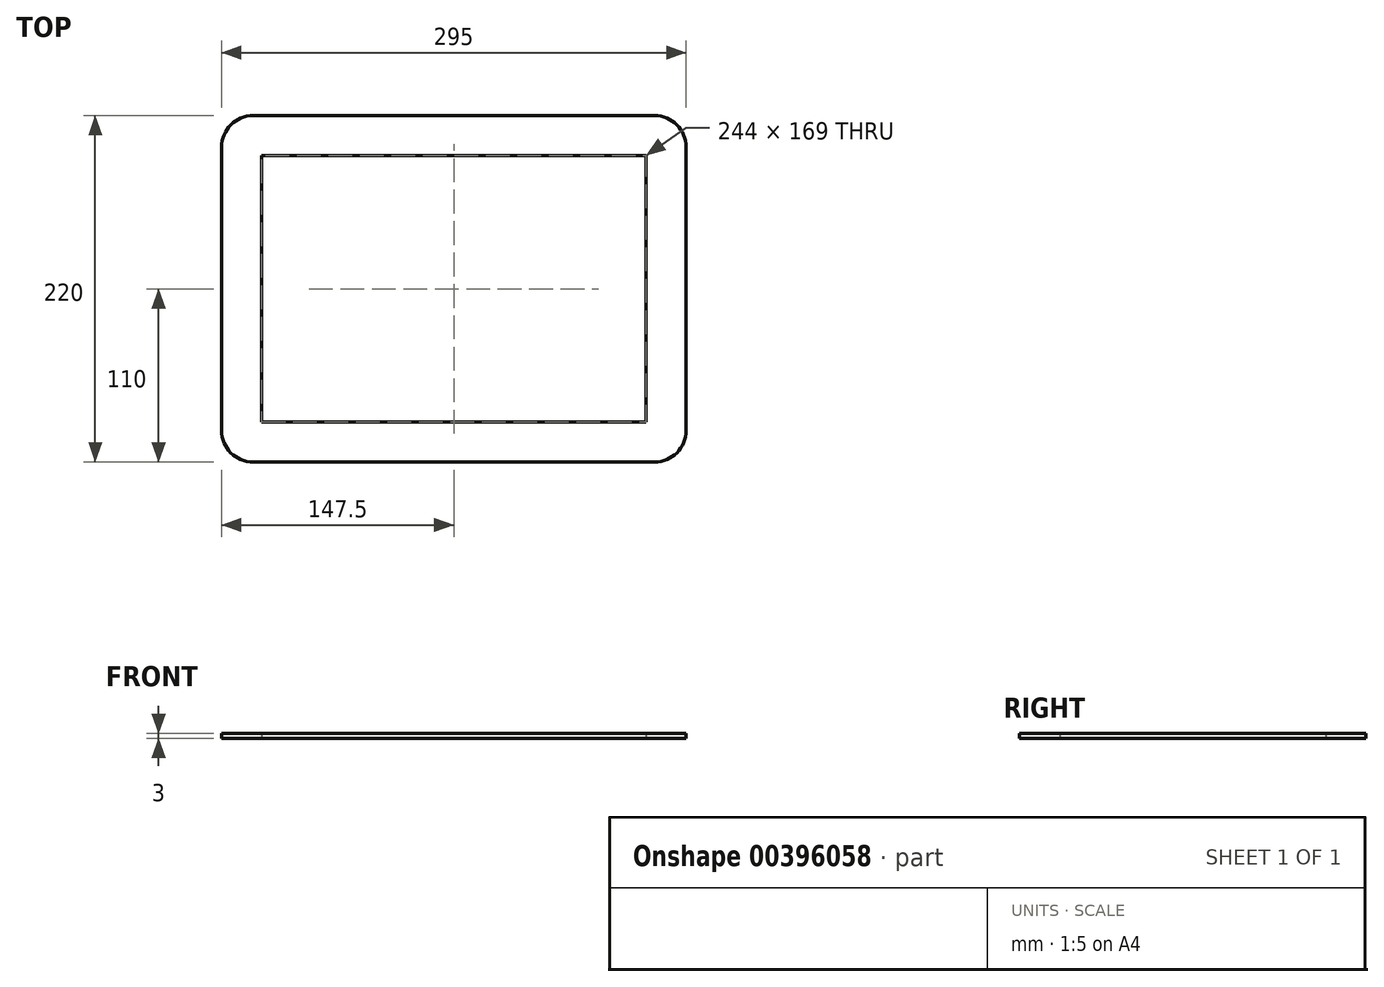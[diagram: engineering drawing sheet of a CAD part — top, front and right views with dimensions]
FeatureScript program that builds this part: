
annotation { "Feature Type Name" : "Feature", "Feature Type Description" : "" }
export const myFeature = defineFeature(function(context is Context, id is Id, definition is map)
    precondition{}
    {
        {
            var Q0;
            Q0=qCreatedBy(makeId("Top.planeOp"),FACE);
            var sketch = newSketch(context, id + "F0", { "sketchPlane" : qUnion([Q0])});
            skLineSegment(sketch, "E0.bottom", {"start": v(-127.5, 110) * mm, "end": v(127.5, 110) * mm});
            skLineSegment(sketch, "E0.top", {"start": v(-127.5, -110) * mm, "end": v(127.5, -110) * mm});
            skLineSegment(sketch, "E0.left", {"start": v(-147.5, 90) * mm, "end": v(-147.5, -90) * mm});
            skLineSegment(sketch, "E0.right", {"start": v(147.5, 90) * mm, "end": v(147.5, -90) * mm});
            skPoint(sketch, "E0.middle", {"position": v(0, 0) * mm});
            skPoint(sketch, "E1.visualSharp", {"position": v(-147.5, 110) * mm});
            skArc(sketch, "E1.filletArc", {"start": v(-127.5, 110) * mm, "mid": v(-141.64, 104.14) * mm, "end": v(-147.5, 90) * mm});
            skPoint(sketch, "E2.visualSharp", {"position": v(-147.5, -110) * mm});
            skArc(sketch, "E2.filletArc", {"start": v(-147.5, -90) * mm, "mid": v(-141.64, -104.14) * mm, "end": v(-127.5, -110) * mm});
            skPoint(sketch, "E3.visualSharp", {"position": v(147.5, -110) * mm});
            skArc(sketch, "E3.filletArc", {"start": v(127.5, -110) * mm, "mid": v(141.64, -104.14) * mm, "end": v(147.5, -90) * mm});
            skPoint(sketch, "E4.visualSharp", {"position": v(147.5, 110) * mm});
            skArc(sketch, "E4.filletArc", {"start": v(147.5, 90) * mm, "mid": v(141.64, 104.14) * mm, "end": v(127.5, 110) * mm});
            skLineSegment(sketch, "E5.bottom", {"start": v(-122, 84.5) * mm, "end": v(122, 84.5) * mm});
            skLineSegment(sketch, "E5.top", {"start": v(-122, -84.5) * mm, "end": v(122, -84.5) * mm});
            skLineSegment(sketch, "E5.left", {"start": v(-122, 84.5) * mm, "end": v(-122, -84.5) * mm});
            skLineSegment(sketch, "E5.right", {"start": v(122, 84.5) * mm, "end": v(122, -84.5) * mm});
            skSolve(sketch);
        }
        {
            var Q0;
            Q0=qSketchRegion(id+"F0",true);
            extrude(context, id + "F1", {"entities" : qUnion([Q0]), "depth" : 3 * mm});
        }
    });
